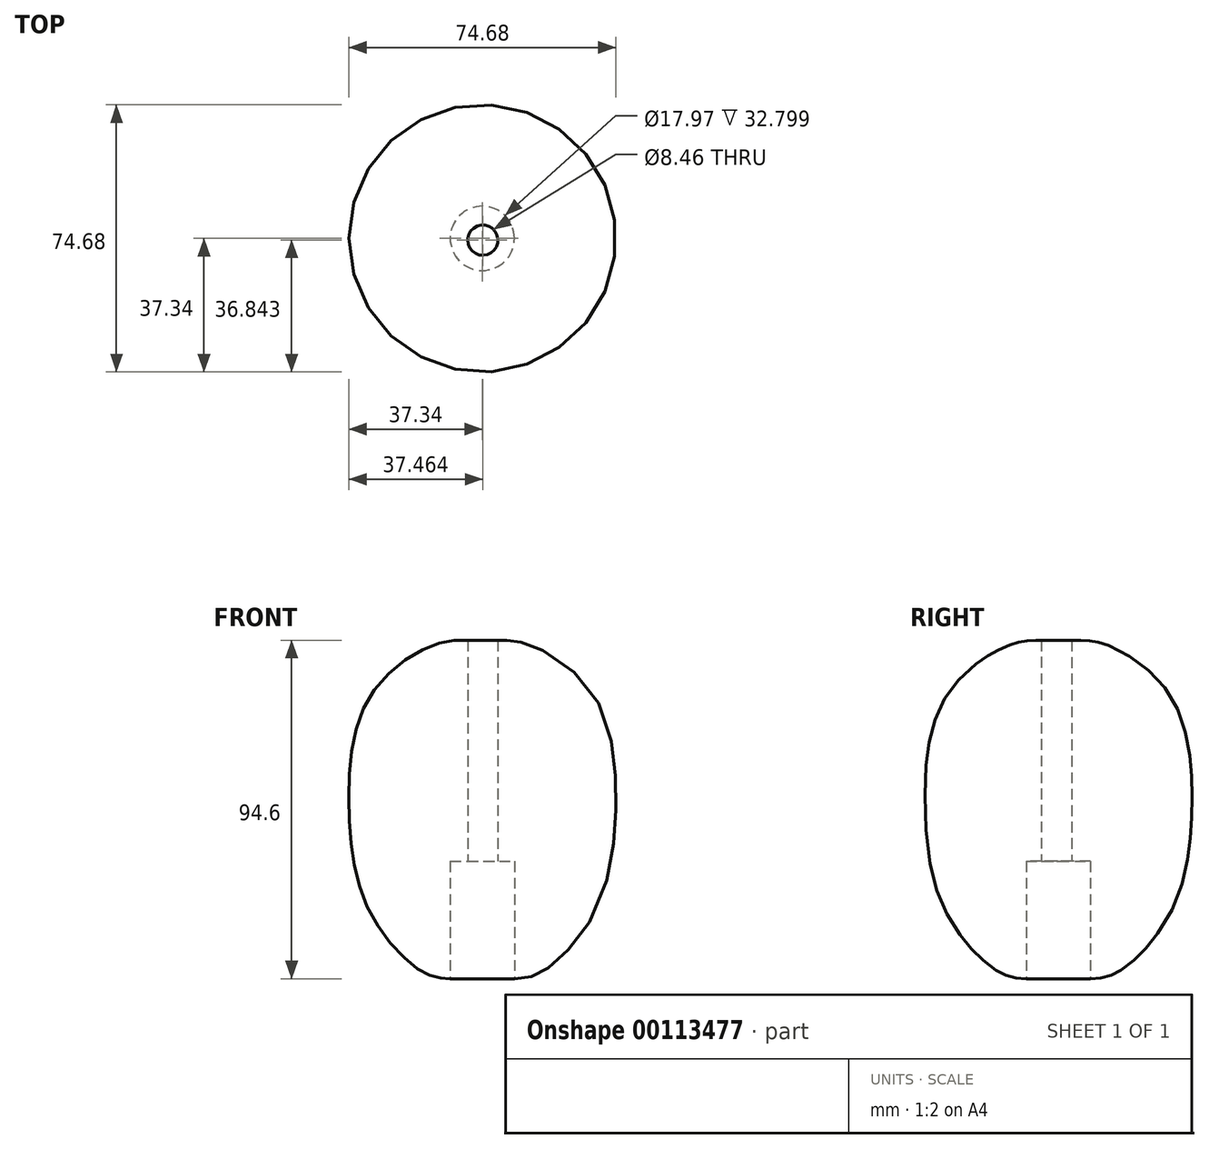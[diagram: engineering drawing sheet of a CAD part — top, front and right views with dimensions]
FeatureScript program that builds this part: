
annotation { "Feature Type Name" : "Feature", "Feature Type Description" : "" }
export const myFeature = defineFeature(function(context is Context, id is Id, definition is map)
    precondition{}
    {
        {
            var Q0;
            Q0=qCreatedBy(makeId("Front.planeOp"),FACE);
            var sketch = newSketch(context, id + "F0", { "sketchPlane" : qUnion([Q0])});
            skLineSegment(sketch, "E0", {"start": v(0, 80.71) * mm, "end": v(-8.99, 80.71) * mm});
            skLineSegment(sketch, "E1", {"start": v(-8.99, 80.71) * mm, "end": v(-8.99, 47.91) * mm});
            skLineSegment(sketch, "E2", {"start": v(0, 80.71) * mm, "end": v(0, 141.84) * mm});
            skFitSpline(sketch, "E3", {"points": [v(0, 141.84) * mm, v(-11.47, 141.84) * mm, v(-31.35, 126.93) * mm, v(-37.31, 96.12) * mm, v(-31.35, 66.3) * mm, v(-15.94, 49.4) * mm, v(-8.99, 47.91) * mm], "startDerivative": vector(-83.92, 13.95) * mm, "endDerivative": vector(64.68, -1.72) * mm});
            skSolve(sketch);
        }
        {
            var Q0;
            Q0 = qSketchRegion(id + "F0", true);
            var Q1;
            Q1=sQuery(id+"F0.wireOp",EDGE,"E2");
            revolve(context, id + "F1", {"entities" : qUnion([Q0]), "axis" : qUnion([Q1]), "revolveType" : RevolveType.FULL});
        }
        {
            var Q0;
            Q0=qCreatedBy(makeId("Top.planeOp"),FACE);
            var sketch = newSketch(context, id + "F2", { "sketchPlane" : qUnion([Q0])});
            skCircle(sketch, "E4", {"center": v(0.12, -0.5) * mm, "radius": 4.23 * mm});
            skSolve(sketch);
        }
        {
            var Q0;
            Q0=makeQuery(id+"F2.imprint","IMPRINT",FACE,{"disambiguationData":[TD([[makeQuery(id+"F2.imprint","IMPRINT",EDGE,{"derivedFrom":sQuery(id+"F2.wireOp",EDGE,"E4")}),1.0]])]});
            extrude(context, id + "F3", {"entities" : qUnion([Q0]), "operationType" : NewBodyOperationType.REMOVE, "depth" : 184.48 * mm});
        }
    });
